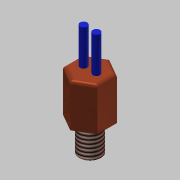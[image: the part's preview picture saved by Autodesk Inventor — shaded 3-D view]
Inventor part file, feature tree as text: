
AUTODESK INVENTOR PART (.ipt)
format: ipt  version: 2014 (Build 180170000, 170)  size: 115,712 bytes
history: native  units: mm
features: extrude x3, sketch x3, fillet x1, thread x1, reference x1
ambient origin geometry x8: Origin, YZ Plane, XZ Plane, XY Plane, X Axis, Y Axis, Z Axis, Center Point
bodies: Solid1 (feature_tree), Solid2 (feature_tree)
feature tree (9):
  extrude  "Extrusion1"  Depth=6.0mm TaperAngle=0.0deg
  fillet  "Fillet1"  Radius=0.5mm
  extrude  "Extrusion2"  Depth=1.0mm
  extrude  "Extrusion3"  Depth=10.0mm
  thread  "Thread1"  [1 undecoded]
  sketch  "Sketch1"  dims[d0=2.4mm d1=6.0mm d2=0.0mm d3=0.5mm]
  reference  "Reference1"
  sketch  "Sketch2"  dims[d4=1.0mm d5=1.0mm]
  sketch  "Sketch3"  dims[d6=1.0mm d7=1.0mm d8=5.0mm d9=0.0mm d10=3.0mm d11=4.0mm d12=0.0mm d13=10.0mm d14=0.0mm]
note: 1 required parameter value undecoded (feature->parameter linkage not recoverable at this tier; creation-order binding heuristic only, values carry confidence <= 0.55)
